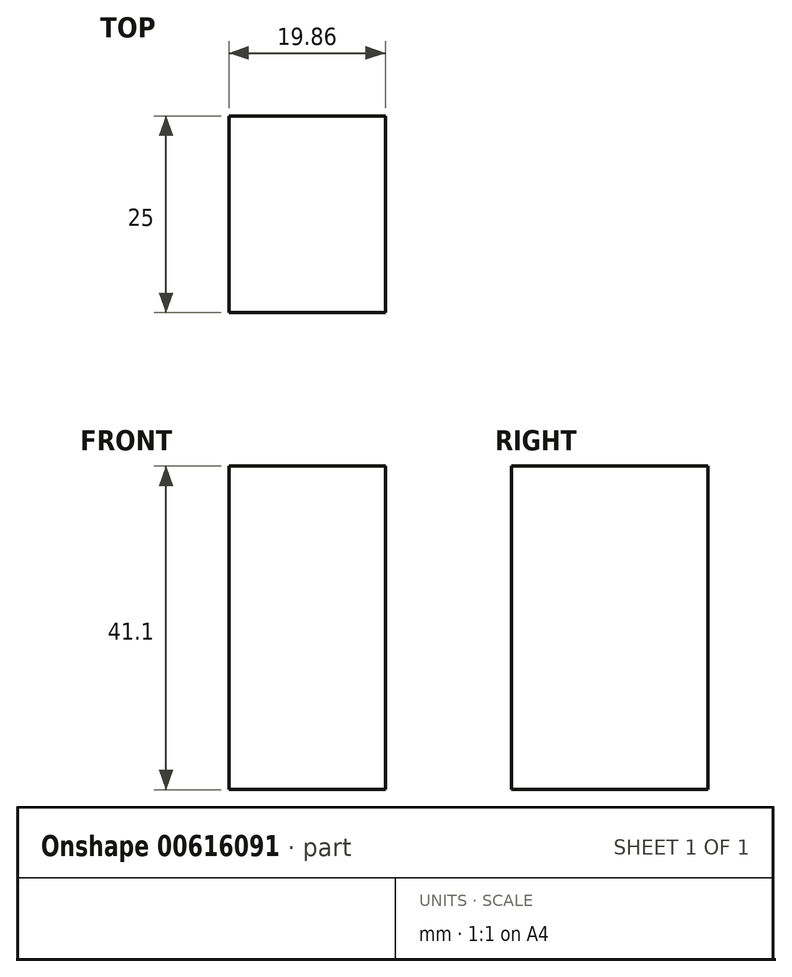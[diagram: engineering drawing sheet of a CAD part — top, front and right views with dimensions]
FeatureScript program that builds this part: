
annotation { "Feature Type Name" : "Feature", "Feature Type Description" : "" }
export const myFeature = defineFeature(function(context is Context, id is Id, definition is map)
    precondition{}
    {
        {
            var Q0;
            Q0=qCreatedBy(makeId("Front.planeOp"),FACE);
            var sketch = newSketch(context, id + "F0", { "sketchPlane" : qUnion([Q0])});
            skLineSegment(sketch, "E0.bottom", {"start": v(-19.86, 20.34) * mm, "end": v(0, 20.34) * mm});
            skLineSegment(sketch, "E0.top", {"start": v(-19.86, -20.76) * mm, "end": v(0, -20.76) * mm});
            skLineSegment(sketch, "E0.left", {"start": v(-19.86, 20.34) * mm, "end": v(-19.86, -20.76) * mm});
            skLineSegment(sketch, "E0.right", {"start": v(0, 20.34) * mm, "end": v(0, -20.76) * mm});
            skLineSegment(sketch, "E1", {"start": v(-19.86, -0.2) * mm, "end": v(0, 0) * mm});
            skLineSegment(sketch, "E2", {"start": v(-19.86, 14.52) * mm, "end": v(0, 14.52) * mm});
            skLineSegment(sketch, "E3.left", {"start": v(-19.86, 20.34) * mm, "end": v(-19.86, 14.52) * mm});
            skLineSegment(sketch, "E3.right", {"start": v(0, 20.34) * mm, "end": v(0, 14.52) * mm});
            skLineSegment(sketch, "E4.top", {"start": v(-19.86, 0) * mm, "end": v(0, 0) * mm});
            skLineSegment(sketch, "E4.left", {"start": v(-19.86, 14.52) * mm, "end": v(-19.86, 0) * mm});
            skLineSegment(sketch, "E4.right", {"start": v(0, 14.52) * mm, "end": v(0, 0) * mm});
            skLineSegment(sketch, "E5.left", {"start": v(-19.86, 0) * mm, "end": v(-19.86, -20.76) * mm});
            skLineSegment(sketch, "E5.right", {"start": v(0, 0) * mm, "end": v(0, -20.76) * mm});
            skSolve(sketch);
        }
        {
            var Q0;
            {var subQ0=sQuery(id+"F0.wireOp",EDGE,"E1");Q0=makeQuery(id+"F0.imprint","IMPRINT",FACE,{"disambiguationData":[TD([[makeQuery(id+"F0.imprint","IMPRINT",EDGE,{"derivedFrom":subQ0}),-1.0]])]});}
            var Q1;
            Q1=makeQuery(id+"F0.imprint","IMPRINT",FACE,{"disambiguationData":[TD([[makeQuery(id+"F0.imprint","IMPRINT",EDGE,{"derivedFrom":sQuery(id+"F0.wireOp",EDGE,"E0.bottom")}),-1.0]])]});
            var Q2;
            Q2=makeQuery(id+"F0.imprint","IMPRINT",FACE,{"disambiguationData":[TD([[makeQuery(id+"F0.imprint","IMPRINT",EDGE,{"derivedFrom":sQuery(id+"F0.wireOp",EDGE,"E2")}),-1.0]])]});
            var Q3;
            {var subQ0=sQuery(id+"F0.wireOp",EDGE,"E1");Q3=makeQuery(id+"F0.imprint","IMPRINT",FACE,{"disambiguationData":[TD([[makeQuery(id+"F0.imprint","IMPRINT",EDGE,{"derivedFrom":subQ0}),1.0]])]});}
            extrude(context, id + "F1", {"entities" : qUnion([Q0, Q1, Q2, Q3]), "depth" : 25 * mm, "offsetDistance" : 25 * mm});
        }
    });
